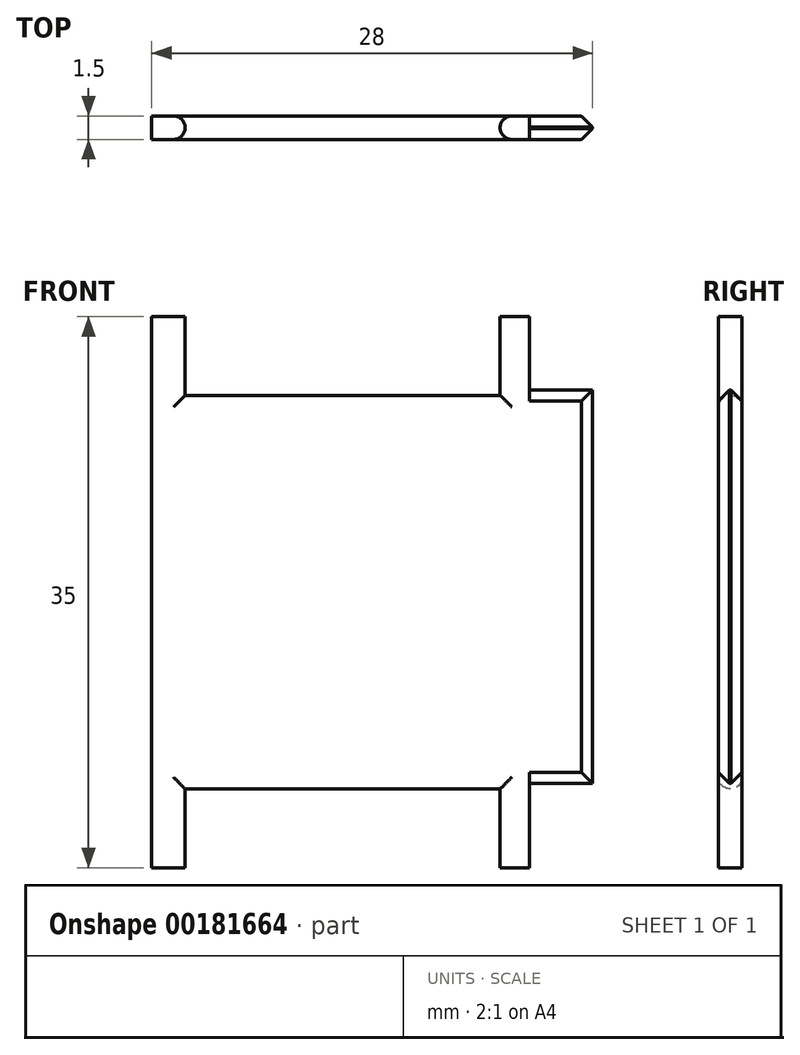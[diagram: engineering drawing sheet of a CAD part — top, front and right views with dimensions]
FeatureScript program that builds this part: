
annotation { "Feature Type Name" : "Feature", "Feature Type Description" : "" }
export const myFeature = defineFeature(function(context is Context, id is Id, definition is map)
    precondition{}
    {
        {
            var Q0;
            Q0=qCreatedBy(makeId("Front.planeOp"),FACE);
            var sketch = newSketch(context, id + "F0", { "sketchPlane" : qUnion([Q0])});
            skLineSegment(sketch, "E0.bottom", {"start": v(-12, 17.5) * mm, "end": v(12, 17.5) * mm});
            skLineSegment(sketch, "E0.top", {"start": v(-12, -17.5) * mm, "end": v(12, -17.5) * mm});
            skLineSegment(sketch, "E0.left", {"start": v(-12, 17.5) * mm, "end": v(-12, -17.5) * mm});
            skLineSegment(sketch, "E0.right", {"start": v(12, 17.5) * mm, "end": v(12, -17.5) * mm});
            skPoint(sketch, "E0.middle", {"position": v(0, 0) * mm});
            skLineSegment(sketch, "E1.bottom", {"start": v(-9.87, 17.5) * mm, "end": v(10.13, 17.5) * mm});
            skLineSegment(sketch, "E1.top", {"start": v(-9.87, 12.5) * mm, "end": v(10.13, 12.5) * mm});
            skLineSegment(sketch, "E1.left", {"start": v(-9.87, 17.5) * mm, "end": v(-9.87, 12.5) * mm});
            skLineSegment(sketch, "E1.right", {"start": v(10.13, 17.5) * mm, "end": v(10.13, 12.5) * mm});
            skLineSegment(sketch, "E2.bottom", {"start": v(-9.87, -17.5) * mm, "end": v(10.13, -17.5) * mm});
            skLineSegment(sketch, "E2.top", {"start": v(-9.87, -12.5) * mm, "end": v(10.13, -12.5) * mm});
            skLineSegment(sketch, "E2.left", {"start": v(-9.87, -17.5) * mm, "end": v(-9.87, -12.5) * mm});
            skLineSegment(sketch, "E2.right", {"start": v(10.13, -17.5) * mm, "end": v(10.13, -12.5) * mm});
            skLineSegment(sketch, "E3.bottom", {"start": v(12, 12.85) * mm, "end": v(16, 12.85) * mm});
            skLineSegment(sketch, "E3.top", {"start": v(12, -12.15) * mm, "end": v(16, -12.15) * mm});
            skLineSegment(sketch, "E3.left", {"start": v(12, 12.85) * mm, "end": v(12, -12.15) * mm});
            skLineSegment(sketch, "E3.right", {"start": v(16, 12.85) * mm, "end": v(16, -12.15) * mm});
            skSolve(sketch);
        }
        {
            var Q0;
            {var subQ0=sQuery(id+"F0.wireOp",EDGE,"E0.left");Q0=makeQuery(id+"F0.imprint","IMPRINT",FACE,{"disambiguationData":[TD([[makeQuery(id+"F0.imprint","IMPRINT",EDGE,{"derivedFrom":subQ0}),1.0]])]});}
            var Q1;
            Q1=makeQuery(id+"F0.imprint","IMPRINT",FACE,{"disambiguationData":[TD([[makeQuery(id+"F0.imprint","IMPRINT",EDGE,{"derivedFrom":sQuery(id+"F0.wireOp",EDGE,"E3.bottom")}),-1.0]])]});
            extrude(context, id + "F1", {"entities" : qUnion([Q0, Q1]), "depth" : 1.5 * mm});
        }
        {
            var Q0;
            Q0=makeQuery(id+"F1.opExtrude","CAP_EDGE",EDGE,{"disambiguationData":[OSD([sQuery(id+"F0.wireOp",EDGE,"E1.top")])],"isStart":false});
            var Q1;
            Q1=makeQuery(id+"F1.opExtrude","CAP_EDGE",EDGE,{"disambiguationData":[OSD([sQuery(id+"F0.wireOp",EDGE,"E2.top")])],"isStart":false});
            var Q2;
            Q2=makeQuery(id+"F1.opExtrude","CAP_EDGE",EDGE,{"disambiguationData":[OSD([sQuery(id+"F0.wireOp",EDGE,"E2.top")])],"isStart":true});
            var Q3;
            Q3=makeQuery(id+"F1.opExtrude","CAP_EDGE",EDGE,{"disambiguationData":[OSD([sQuery(id+"F0.wireOp",EDGE,"E1.top")])],"isStart":true});
            var Q4;
            Q4=makeQuery(id+"F1.opExtrude","CAP_EDGE",EDGE,{"disambiguationData":[OSD([sQuery(id+"F0.wireOp",EDGE,"E1.right")])],"isStart":true});
            var Q5;
            Q5=makeQuery(id+"F1.opExtrude","CAP_EDGE",EDGE,{"disambiguationData":[OSD([sQuery(id+"F0.wireOp",EDGE,"E1.left")])],"isStart":true});
            var Q6;
            Q6=makeQuery(id+"F1.opExtrude","CAP_EDGE",EDGE,{"disambiguationData":[OSD([sQuery(id+"F0.wireOp",EDGE,"E1.left")])],"isStart":false});
            var Q7;
            Q7=makeQuery(id+"F1.opExtrude","CAP_EDGE",EDGE,{"disambiguationData":[OSD([sQuery(id+"F0.wireOp",EDGE,"E2.left")])],"isStart":false});
            var Q8;
            Q8=makeQuery(id+"F1.opExtrude","CAP_EDGE",EDGE,{"disambiguationData":[OSD([sQuery(id+"F0.wireOp",EDGE,"E2.left")])],"isStart":true});
            var Q9;
            Q9=makeQuery(id+"F1.opExtrude","CAP_EDGE",EDGE,{"disambiguationData":[OSD([sQuery(id+"F0.wireOp",EDGE,"E2.right")])],"isStart":false});
            var Q10;
            Q10=makeQuery(id+"F1.opExtrude","CAP_EDGE",EDGE,{"disambiguationData":[OSD([sQuery(id+"F0.wireOp",EDGE,"E2.right")])],"isStart":true});
            var Q11;
            Q11=makeQuery(id+"F1.opExtrude","CAP_EDGE",EDGE,{"disambiguationData":[OSD([sQuery(id+"F0.wireOp",EDGE,"E1.right")])],"isStart":false});
            fillet(context, id + "F2", {"entities" : qUnion([Q0, Q1, Q2, Q3, Q4, Q5, Q6, Q7, Q8, Q9, Q10, Q11]), "radius" : 0.75 * mm, "tangentPropagation" : true, "allowEdgeOverflow" : false});
        }
        {
            var Q0;
            Q0=makeQuery(id+"F1.opExtrude","CAP_EDGE",EDGE,{"disambiguationData":[OSD([sQuery(id+"F0.wireOp",EDGE,"E3.right")])],"isStart":false});
            var Q1;
            Q1=makeQuery(id+"F1.opExtrude","CAP_EDGE",EDGE,{"disambiguationData":[OSD([sQuery(id+"F0.wireOp",EDGE,"E3.right")])],"isStart":true});
            var Q2;
            Q2=makeQuery(id+"F1.opExtrude","CAP_EDGE",EDGE,{"disambiguationData":[OSD([sQuery(id+"F0.wireOp",EDGE,"E3.top")])],"isStart":false});
            var Q3;
            Q3=makeQuery(id+"F1.opExtrude","CAP_EDGE",EDGE,{"disambiguationData":[OSD([sQuery(id+"F0.wireOp",EDGE,"E3.top")])],"isStart":true});
            var Q4;
            Q4=makeQuery(id+"F1.opExtrude","CAP_EDGE",EDGE,{"disambiguationData":[OSD([sQuery(id+"F0.wireOp",EDGE,"E3.bottom")])],"isStart":true});
            var Q5;
            Q5=makeQuery(id+"F1.opExtrude","CAP_EDGE",EDGE,{"disambiguationData":[OSD([sQuery(id+"F0.wireOp",EDGE,"E3.bottom")])],"isStart":false});
            chamfer(context, id + "F3", {"entities" : qUnion([Q0, Q1, Q2, Q3, Q4, Q5]), "width" : 0.7 * mm, "tangentPropagation" : true});
        }
    });
